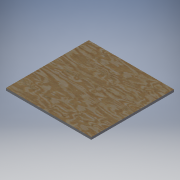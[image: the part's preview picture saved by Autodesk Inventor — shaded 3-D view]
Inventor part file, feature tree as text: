
AUTODESK INVENTOR PART (.ipt)
format: ipt  version: 2018.2 (Build 222227000, 227)  size: 121,856 bytes
history: native  units: in
note: dims shown in document units (in); Inventor stores cm internally (conversion verified against a paired STEP export)
features: extrude x1, sketch x1
ambient origin geometry x8: Origin, YZ Plane, XZ Plane, XY Plane, X Axis, Y Axis, Z Axis, Center Point
bodies: Solid1 (feature_tree)
feature tree (2):
  extrude  "Extrusion1"  Depth=0.75in
  sketch  "Sketch1"  dims[d0=28.226in d1=0.75in d2=27.398in d3=0.0in]
